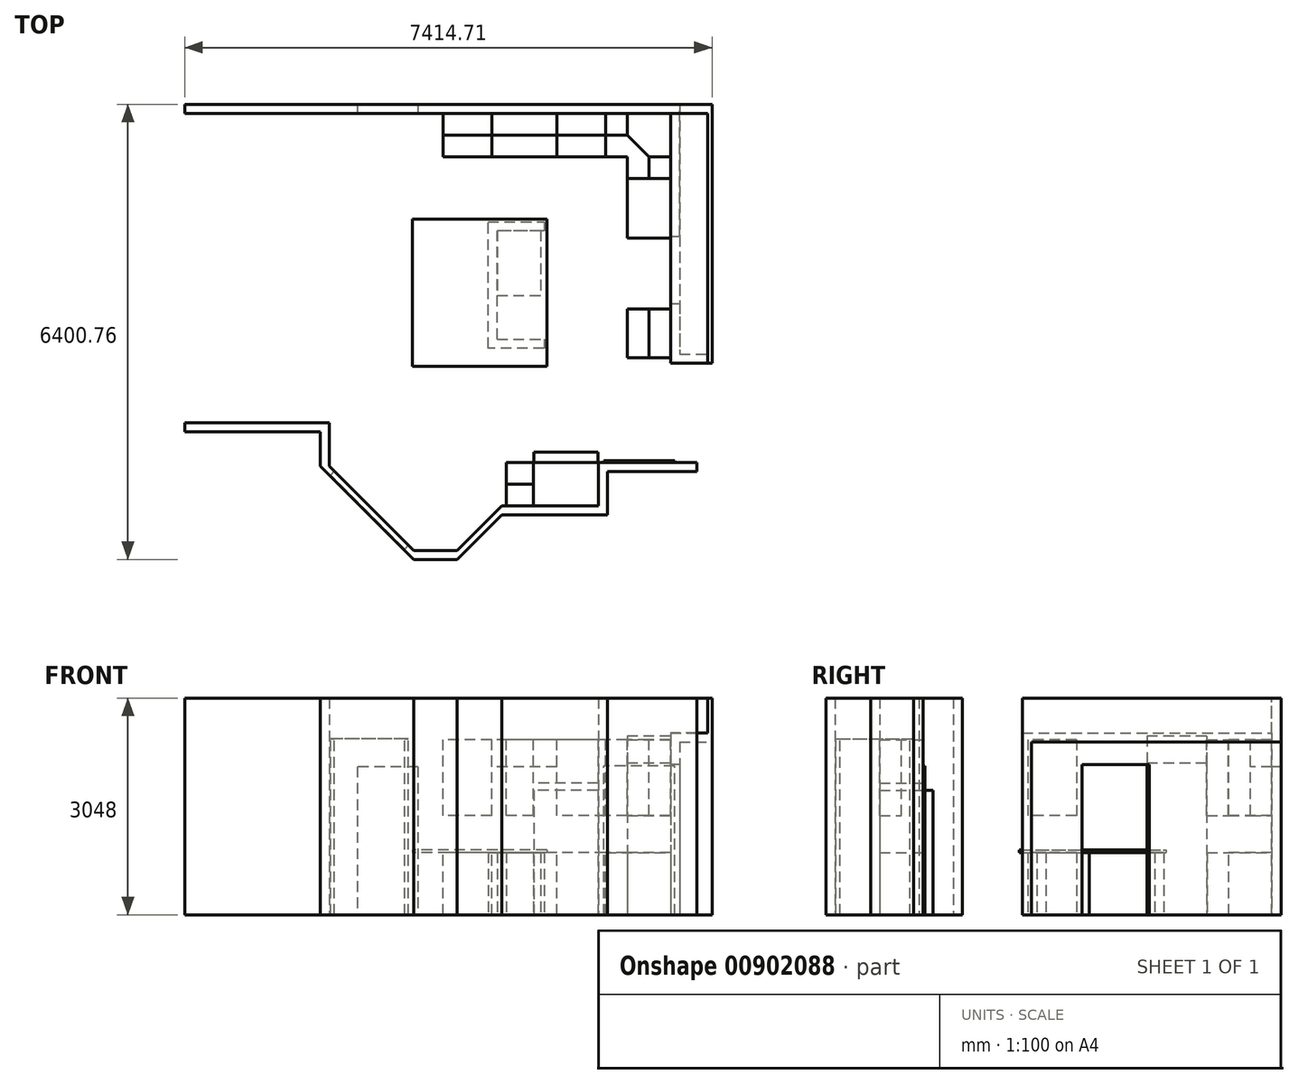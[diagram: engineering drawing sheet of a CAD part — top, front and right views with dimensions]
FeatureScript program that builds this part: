
annotation { "Feature Type Name" : "Feature", "Feature Type Description" : "" }
export const myFeature = defineFeature(function(context is Context, id is Id, definition is map)
    precondition{}
    {
        {
            var Q0;
            Q0=qCreatedBy(makeId("Top.planeOp"),FACE);
            var sketch = newSketch(context, id + "F0", { "sketchPlane" : qUnion([Q0])});
            skLineSegment(sketch, "E0.bottom", {"start": v(1769.95, -316.58) * mm, "end": v(-1786.05, -316.58) * mm});
            skLineSegment(sketch, "E0.top", {"start": v(1769.95, -189.58) * mm, "end": v(-1786.05, -189.58) * mm});
            skLineSegment(sketch, "E0.left", {"start": v(1769.95, -316.58) * mm, "end": v(1769.95, -189.58) * mm});
            skLineSegment(sketch, "E0.right", {"start": v(-1786.05, -316.58) * mm, "end": v(-1786.05, -189.58) * mm});
            skSolve(sketch);
        }
        {
            var Q0;
            Q0=qSketchRegion(id+"F0",true);
            extrude(context, id + "F1", {"entities" : qUnion([Q0]), "depth" : 3048 * mm, "offsetDistance" : 25.4 * mm});
        }
        {
            var Q0;
            Q0=makeQuery(id+"F1.opExtrude","CAP_FACE",FACE,{"disambiguationData":[OSD([sQuery(id+"F0.wireOp",EDGE,"E0.bottom"),sQuery(id+"F0.wireOp",EDGE,"E0.top"),sQuery(id+"F0.wireOp",EDGE,"E0.left"),sQuery(id+"F0.wireOp",EDGE,"E0.right")])],"isStart":true});
            var sketch = newSketch(context, id + "F2", { "sketchPlane" : qUnion([Q0])});
            skLineSegment(sketch, "E1", {"start": v(1769.95, 316.58) * mm, "end": v(1769.95, 2043.78) * mm});
            skLineSegment(sketch, "E2", {"start": v(1769.95, 2043.78) * mm, "end": v(1896.95, 2043.78) * mm});
            skLineSegment(sketch, "E3", {"start": v(1896.95, 2043.78) * mm, "end": v(1896.95, 189.58) * mm});
            skLineSegment(sketch, "E4", {"start": v(1896.95, 189.58) * mm, "end": v(1769.95, 189.58) * mm});
            skLineSegment(sketch, "E5", {"start": v(1769.95, 189.58) * mm, "end": v(1769.95, 316.58) * mm});
            skSolve(sketch);
        }
        {
            var Q0;
            Q0=makeQuery(id+"F2.imprint","IMPRINT",FACE,{"disambiguationData":[TD([[makeQuery(id+"F2.imprint","IMPRINT",EDGE,{"derivedFrom":sQuery(id+"F2.wireOp",EDGE,"E1")}),-1.0]])]});
            var Q1;
            Q1=makeQuery(id+"F1.opExtrude","CAP_FACE",FACE,{"disambiguationData":[OSD([sQuery(id+"F0.wireOp",EDGE,"E0.bottom"),sQuery(id+"F0.wireOp",EDGE,"E0.top"),sQuery(id+"F0.wireOp",EDGE,"E0.left"),sQuery(id+"F0.wireOp",EDGE,"E0.right")])],"isStart":false});
            extrude(context, id + "F3", {"entities" : qUnion([Q0]), "operationType" : NewBodyOperationType.ADD, "endBound" : BoundingType.UP_TO_SURFACE, "oppositeDirection" : true, "depth" : 25.4 * mm, "endBoundEntityFace" : qUnion([Q1]), "offsetDistance" : 25.4 * mm});
        }
        {
            var Q0;
            Q0=makeQuery(id+"F3.boolean.opBoolean","MERGE",FACE,{"derivedFrom":[makeQuery(id+"F1.opExtrude","CAP_FACE",FACE,{"disambiguationData":[OSD([sQuery(id+"F0.wireOp",EDGE,"E0.bottom"),sQuery(id+"F0.wireOp",EDGE,"E0.top"),sQuery(id+"F0.wireOp",EDGE,"E0.left"),sQuery(id+"F0.wireOp",EDGE,"E0.right")])],"isStart":true}),makeQuery(id+"F3.opExtrude","CAP_FACE",FACE,{"disambiguationData":[OSD([sQuery(id+"F2.wireOp",EDGE,"E1"),sQuery(id+"F2.wireOp",EDGE,"E2"),sQuery(id+"F2.wireOp",EDGE,"E3"),sQuery(id+"F2.wireOp",EDGE,"E4"),sQuery(id+"F2.wireOp",EDGE,"E5")])],"isStart":true})]});
            var sketch = newSketch(context, id + "F4", { "sketchPlane" : qUnion([Q0])});
            skLineSegment(sketch, "E6", {"start": v(1769.95, 2043.78) * mm, "end": v(1769.95, 3936.08) * mm, "construction": true});
            skLineSegment(sketch, "E7", {"start": v(1896.95, 2043.78) * mm, "end": v(1896.95, 4648.91) * mm, "construction": true});
            skLineSegment(sketch, "E8.bottom", {"start": v(1769.95, 2989.93) * mm, "end": v(1896.95, 2989.93) * mm});
            skLineSegment(sketch, "E8.top", {"start": v(1769.95, 3828.13) * mm, "end": v(1896.95, 3828.13) * mm});
            skLineSegment(sketch, "E8.left", {"start": v(1769.95, 2989.93) * mm, "end": v(1769.95, 3828.13) * mm});
            skLineSegment(sketch, "E8.right", {"start": v(1896.95, 2989.93) * mm, "end": v(1896.95, 3828.13) * mm});
            skSolve(sketch);
        }
        {
            var Q0;
            Q0=qSketchRegion(id+"F4",true);
            var Q1;
            Q1=makeQuery(id+"F3.boolean.opBoolean","MERGE",FACE,{"derivedFrom":[makeQuery(id+"F1.opExtrude","CAP_FACE",FACE,{"disambiguationData":[OSD([sQuery(id+"F0.wireOp",EDGE,"E0.bottom"),sQuery(id+"F0.wireOp",EDGE,"E0.top"),sQuery(id+"F0.wireOp",EDGE,"E0.left"),sQuery(id+"F0.wireOp",EDGE,"E0.right")])],"isStart":false}),makeQuery(id+"F3.opExtrude","CAP_FACE",FACE,{"disambiguationData":[OSD([sQuery(id+"F2.wireOp",EDGE,"E1"),sQuery(id+"F2.wireOp",EDGE,"E2"),sQuery(id+"F2.wireOp",EDGE,"E3"),sQuery(id+"F2.wireOp",EDGE,"E4"),sQuery(id+"F2.wireOp",EDGE,"E5")])],"isStart":false})]});
            extrude(context, id + "F5", {"entities" : qUnion([Q0]), "endBound" : BoundingType.UP_TO_SURFACE, "oppositeDirection" : true, "depth" : 25.4 * mm, "endBoundEntityFace" : qUnion([Q1]), "offsetDistance" : 25.4 * mm});
        }
        {
            var Q0;
            Q0=makeQuery(id+"F3.boolean.opBoolean","MERGE",FACE,{"derivedFrom":[makeQuery(id+"F1.opExtrude","CAP_FACE",FACE,{"disambiguationData":[OSD([sQuery(id+"F0.wireOp",EDGE,"E0.bottom"),sQuery(id+"F0.wireOp",EDGE,"E0.top"),sQuery(id+"F0.wireOp",EDGE,"E0.left"),sQuery(id+"F0.wireOp",EDGE,"E0.right")])],"isStart":true}),makeQuery(id+"F3.opExtrude","CAP_FACE",FACE,{"disambiguationData":[OSD([sQuery(id+"F2.wireOp",EDGE,"E1"),sQuery(id+"F2.wireOp",EDGE,"E2"),sQuery(id+"F2.wireOp",EDGE,"E3"),sQuery(id+"F2.wireOp",EDGE,"E4"),sQuery(id+"F2.wireOp",EDGE,"E5")])],"isStart":true})]});
            var sketch = newSketch(context, id + "F6", { "sketchPlane" : qUnion([Q0])});
            skLineSegment(sketch, "E9", {"start": v(1769.95, 2043.78) * mm, "end": v(1769.95, 3749.14) * mm, "construction": true});
            skLineSegment(sketch, "E10.bottom", {"start": v(1769.95, 5352.13) * mm, "end": v(753.95, 5352.13) * mm});
            skLineSegment(sketch, "E10.top", {"start": v(1769.95, 5225.13) * mm, "end": v(753.95, 5225.13) * mm});
            skLineSegment(sketch, "E10.left", {"start": v(1769.95, 5225.13) * mm, "end": v(1769.95, 5352.13) * mm});
            skLineSegment(sketch, "E10.right", {"start": v(753.95, 5225.13) * mm, "end": v(753.95, 5352.13) * mm});
            skSolve(sketch);
        }
        {
            var Q0;
            Q0=makeQuery(id+"F6.imprint","IMPRINT",FACE,{"disambiguationData":[TD([[makeQuery(id+"F6.imprint","IMPRINT",EDGE,{"derivedFrom":sQuery(id+"F6.wireOp",EDGE,"E10.bottom")}),1.0]])]});
            var Q1;
            Q1=makeQuery(id+"F3.boolean.opBoolean","MERGE",FACE,{"derivedFrom":[makeQuery(id+"F1.opExtrude","CAP_FACE",FACE,{"disambiguationData":[OSD([sQuery(id+"F0.wireOp",EDGE,"E0.bottom"),sQuery(id+"F0.wireOp",EDGE,"E0.top"),sQuery(id+"F0.wireOp",EDGE,"E0.left"),sQuery(id+"F0.wireOp",EDGE,"E0.right")])],"isStart":false}),makeQuery(id+"F3.opExtrude","CAP_FACE",FACE,{"disambiguationData":[OSD([sQuery(id+"F2.wireOp",EDGE,"E1"),sQuery(id+"F2.wireOp",EDGE,"E2"),sQuery(id+"F2.wireOp",EDGE,"E3"),sQuery(id+"F2.wireOp",EDGE,"E4"),sQuery(id+"F2.wireOp",EDGE,"E5")])],"isStart":false})]});
            extrude(context, id + "F7", {"entities" : qUnion([Q0]), "endBound" : BoundingType.UP_TO_SURFACE, "oppositeDirection" : true, "depth" : 25.4 * mm, "endBoundEntityFace" : qUnion([Q1]), "offsetDistance" : 25.4 * mm});
        }
        {
            var Q0;
            Q0=makeQuery(id+"F7.opExtrude","CAP_FACE",FACE,{"disambiguationData":[OSD([sQuery(id+"F6.wireOp",EDGE,"E10.bottom"),sQuery(id+"F6.wireOp",EDGE,"E10.top"),sQuery(id+"F6.wireOp",EDGE,"E10.left"),sQuery(id+"F6.wireOp",EDGE,"E10.right")])],"isStart":true});
            var sketch = newSketch(context, id + "F8", { "sketchPlane" : qUnion([Q0])});
            skLineSegment(sketch, "E11.bottom", {"start": v(753.95, 5225.13) * mm, "end": v(880.95, 5225.13) * mm});
            skLineSegment(sketch, "E11.top", {"start": v(753.95, 5834.73) * mm, "end": v(880.95, 5834.73) * mm});
            skLineSegment(sketch, "E11.left", {"start": v(753.95, 5225.13) * mm, "end": v(753.95, 5834.73) * mm});
            skLineSegment(sketch, "E11.right", {"start": v(880.95, 5225.13) * mm, "end": v(880.95, 5834.73) * mm});
            skLineSegment(sketch, "E12.bottom", {"start": v(880.95, 5834.73) * mm, "end": v(-604.95, 5834.73) * mm});
            skLineSegment(sketch, "E12.top", {"start": v(880.95, 5961.73) * mm, "end": v(-604.95, 5961.73) * mm});
            skLineSegment(sketch, "E12.left", {"start": v(880.95, 5834.73) * mm, "end": v(880.95, 5961.73) * mm});
            skLineSegment(sketch, "E12.right", {"start": v(-604.95, 5834.73) * mm, "end": v(-604.95, 5961.73) * mm});
            skLineSegment(sketch, "E13", {"start": v(-604.95, 5834.73) * mm, "end": v(-1233.57, 6463.34) * mm});
            skLineSegment(sketch, "E14", {"start": v(-1233.57, 6463.34) * mm, "end": v(-1843.17, 6463.34) * mm});
            skLineSegment(sketch, "E15", {"start": v(-1843.17, 6463.34) * mm, "end": v(-1843.17, 6590.34) * mm});
            skLineSegment(sketch, "E16", {"start": v(-1843.17, 6590.34) * mm, "end": v(-1233.57, 6590.34) * mm});
            skLineSegment(sketch, "E17", {"start": v(-1233.57, 6590.34) * mm, "end": v(-604.95, 5961.73) * mm});
            skLineSegment(sketch, "E18", {"start": v(-1843.17, 6463.34) * mm, "end": v(-3028.56, 5277.95) * mm});
            skLineSegment(sketch, "E19", {"start": v(-3028.56, 5277.95) * mm, "end": v(-3028.56, 4668.35) * mm});
            skLineSegment(sketch, "E20", {"start": v(-3028.56, 4668.35) * mm, "end": v(-5060.56, 4668.35) * mm});
            skLineSegment(sketch, "E21", {"start": v(-5060.56, 4668.35) * mm, "end": v(-5060.56, 4795.35) * mm});
            skLineSegment(sketch, "E22", {"start": v(-5060.56, 4795.35) * mm, "end": v(-3155.56, 4795.35) * mm});
            skLineSegment(sketch, "E23", {"start": v(-3155.56, 4795.35) * mm, "end": v(-3155.56, 5277.95) * mm});
            skLineSegment(sketch, "E24", {"start": v(-3155.56, 5277.95) * mm, "end": v(-1843.17, 6590.34) * mm});
            skSolve(sketch);
        }
        {
            var Q0;
            Q0=makeQuery(id+"F8.imprint","IMPRINT",FACE,{"disambiguationData":[TD([[makeQuery(id+"F8.imprint","IMPRINT",EDGE,{"derivedFrom":sQuery(id+"F8.wireOp",EDGE,"E15")}),1.0]])]});
            var Q1;
            Q1=makeQuery(id+"F8.imprint","IMPRINT",FACE,{"disambiguationData":[TD([[makeQuery(id+"F8.imprint","IMPRINT",EDGE,{"derivedFrom":sQuery(id+"F8.wireOp",EDGE,"E12.right")}),1.0]])]});
            var Q2;
            Q2=makeQuery(id+"F8.imprint","IMPRINT",FACE,{"disambiguationData":[TD([[makeQuery(id+"F8.imprint","IMPRINT",EDGE,{"derivedFrom":sQuery(id+"F8.wireOp",EDGE,"E12.top")}),1.0]])]});
            var Q3;
            {var subQ0=sQuery(id+"F8.wireOp",EDGE,"E11.left");var subQ1=makeQuery(id+"F7.opExtrude","CAP_EDGE",EDGE,{"disambiguationData":[OSD([sQuery(id+"F6.wireOp",EDGE,"E10.bottom")])],"isStart":true});var subQ2=makeQuery(id+"F8.imprint","INTERSECT",VERTEX,{"derivedFrom":[subQ1,subQ0]});Q3=makeQuery(id+"F8.imprint","IMPRINT",FACE,{"disambiguationData":[TD([[makeQuery(id+"F8.imprint","IMPRINT",EDGE,{"disambiguationData":[TD([[subQ2,-1.0]])],"derivedFrom":subQ0}),-1.0]])]});}
            var Q4;
            Q4=makeQuery(id+"F5.opExtrude","CAP_FACE",FACE,{"disambiguationData":[OSD([sQuery(id+"F4.wireOp",EDGE,"E8.bottom"),sQuery(id+"F4.wireOp",EDGE,"E8.top"),sQuery(id+"F4.wireOp",EDGE,"E8.left"),sQuery(id+"F4.wireOp",EDGE,"E8.right")])],"isStart":false});
            extrude(context, id + "F9", {"entities" : qUnion([Q0, Q1, Q2, Q3]), "operationType" : NewBodyOperationType.ADD, "endBound" : BoundingType.UP_TO_SURFACE, "oppositeDirection" : true, "depth" : 25.4 * mm, "endBoundEntityFace" : qUnion([Q4]), "offsetDistance" : 25.4 * mm});
        }
        {
            var Q0;
            {var subQ0=sQuery(id+"F6.wireOp",EDGE,"E10.bottom");Q0=makeQuery(id+"F9.boolean.opBoolean","MERGE",FACE,{"derivedFrom":[makeQuery(id+"F7.opExtrude","CAP_FACE",FACE,{"disambiguationData":[OSD([subQ0,sQuery(id+"F6.wireOp",EDGE,"E10.top"),sQuery(id+"F6.wireOp",EDGE,"E10.left"),sQuery(id+"F6.wireOp",EDGE,"E10.right")])],"isStart":true}),makeQuery(id+"F9.opExtrude","CAP_FACE",FACE,{"disambiguationData":[OSD([subQ0,sQuery(id+"F8.wireOp",EDGE,"E11.left"),sQuery(id+"F8.wireOp",EDGE,"E11.right"),sQuery(id+"F8.wireOp",EDGE,"E12.bottom"),sQuery(id+"F8.wireOp",EDGE,"E12.top"),sQuery(id+"F8.wireOp",EDGE,"E12.left"),sQuery(id+"F8.wireOp",EDGE,"E13"),sQuery(id+"F8.wireOp",EDGE,"E14"),sQuery(id+"F8.wireOp",EDGE,"E16"),sQuery(id+"F8.wireOp",EDGE,"E17"),sQuery(id+"F8.wireOp",EDGE,"E18"),sQuery(id+"F8.wireOp",EDGE,"E19"),sQuery(id+"F8.wireOp",EDGE,"E20"),sQuery(id+"F8.wireOp",EDGE,"E21"),sQuery(id+"F8.wireOp",EDGE,"E22"),sQuery(id+"F8.wireOp",EDGE,"E23"),sQuery(id+"F8.wireOp",EDGE,"E24")])],"isStart":true})]});}
            var sketch = newSketch(context, id + "F10", { "sketchPlane" : qUnion([Q0])});
            skLineSegment(sketch, "E25.bottom", {"start": v(1769.95, 5225.13) * mm, "end": v(2138.25, 5225.13) * mm});
            skLineSegment(sketch, "E25.top", {"start": v(1769.95, 5352.13) * mm, "end": v(2138.25, 5352.13) * mm});
            skLineSegment(sketch, "E25.left", {"start": v(1769.95, 5225.13) * mm, "end": v(1769.95, 5352.13) * mm});
            skLineSegment(sketch, "E25.right", {"start": v(2138.25, 5225.13) * mm, "end": v(2138.25, 5352.13) * mm});
            skSolve(sketch);
        }
        {
            var Q0;
            Q0=makeQuery(id+"F10.imprint","IMPRINT",FACE,{"disambiguationData":[TD([[makeQuery(id+"F10.imprint","IMPRINT",EDGE,{"derivedFrom":sQuery(id+"F10.wireOp",EDGE,"E25.bottom")}),1.0]])]});
            var Q1;
            {var subQ0=sQuery(id+"F6.wireOp",EDGE,"E10.bottom");Q1=makeQuery(id+"F9.boolean.opBoolean","MERGE",FACE,{"derivedFrom":[makeQuery(id+"F7.opExtrude","CAP_FACE",FACE,{"disambiguationData":[OSD([subQ0,sQuery(id+"F6.wireOp",EDGE,"E10.top"),sQuery(id+"F6.wireOp",EDGE,"E10.left"),sQuery(id+"F6.wireOp",EDGE,"E10.right")])],"isStart":false}),makeQuery(id+"F9.opExtrude","CAP_FACE",FACE,{"disambiguationData":[OSD([subQ0,sQuery(id+"F8.wireOp",EDGE,"E11.left"),sQuery(id+"F8.wireOp",EDGE,"E11.right"),sQuery(id+"F8.wireOp",EDGE,"E12.bottom"),sQuery(id+"F8.wireOp",EDGE,"E12.top"),sQuery(id+"F8.wireOp",EDGE,"E12.left"),sQuery(id+"F8.wireOp",EDGE,"E13"),sQuery(id+"F8.wireOp",EDGE,"E14"),sQuery(id+"F8.wireOp",EDGE,"E16"),sQuery(id+"F8.wireOp",EDGE,"E17"),sQuery(id+"F8.wireOp",EDGE,"E18"),sQuery(id+"F8.wireOp",EDGE,"E19"),sQuery(id+"F8.wireOp",EDGE,"E20"),sQuery(id+"F8.wireOp",EDGE,"E21"),sQuery(id+"F8.wireOp",EDGE,"E22"),sQuery(id+"F8.wireOp",EDGE,"E23"),sQuery(id+"F8.wireOp",EDGE,"E24")])],"isStart":false})]});}
            extrude(context, id + "F11", {"entities" : qUnion([Q0]), "operationType" : NewBodyOperationType.ADD, "endBound" : BoundingType.UP_TO_SURFACE, "oppositeDirection" : true, "depth" : 25.4 * mm, "endBoundEntityFace" : qUnion([Q1]), "offsetDistance" : 25.4 * mm});
        }
        {
            var Q0;
            Q0=makeQuery(id+"F11.boolean.opBoolean","MERGE",FACE,{"derivedFrom":[makeQuery(id+"F7.opExtrude","SWEPT_FACE",FACE,{"disambiguationData":[OSD([sQuery(id+"F6.wireOp",EDGE,"E10.top")])]}),makeQuery(id+"F11.opExtrude","SWEPT_FACE",FACE,{"disambiguationData":[OSD([sQuery(id+"F10.wireOp",EDGE,"E25.bottom")])]})]});
            var sketch = newSketch(context, id + "F12", { "sketchPlane" : qUnion([Q0])});
            skLineSegment(sketch, "E26.bottom", {"start": v(-1827.1, 0) * mm, "end": v(-830.15, 0) * mm});
            skLineSegment(sketch, "E26.top", {"start": v(-1827.1, 2095.5) * mm, "end": v(-830.15, 2095.5) * mm});
            skLineSegment(sketch, "E26.left", {"start": v(-1827.1, 0) * mm, "end": v(-1827.1, 2095.5) * mm});
            skLineSegment(sketch, "E26.right", {"start": v(-830.15, 0) * mm, "end": v(-830.15, 2095.5) * mm});
            skSolve(sketch);
        }
        {
            var Q0;
            Q0=qSketchRegion(id+"F12",true);
            extrude(context, id + "F13", {"entities" : qUnion([Q0]), "operationType" : NewBodyOperationType.ADD, "depth" : 25.4 * mm, "offsetDistance" : 25.4 * mm});
        }
        {
            var Q0;
            Q0=makeQuery(id+"F1.opExtrude","SWEPT_FACE",FACE,{"disambiguationData":[OSD([sQuery(id+"F0.wireOp",EDGE,"E0.bottom")])]});
            var sketch = newSketch(context, id + "F14", { "sketchPlane" : qUnion([Q0])});
            skLineSegment(sketch, "E27.bottom", {"start": v(-1786.05, 3048) * mm, "end": v(-2636.95, 3048) * mm});
            skLineSegment(sketch, "E27.top", {"start": v(-1786.05, 2082.8) * mm, "end": v(-2636.95, 2082.8) * mm});
            skLineSegment(sketch, "E27.left", {"start": v(-1786.05, 3048) * mm, "end": v(-1786.05, 2082.8) * mm});
            skLineSegment(sketch, "E27.right", {"start": v(-2636.95, 3048) * mm, "end": v(-2636.95, 2082.8) * mm});
            skSolve(sketch);
        }
        {
            var Q0;
            Q0=makeQuery(id+"F14.imprint","IMPRINT",FACE,{"disambiguationData":[TD([[makeQuery(id+"F14.imprint","IMPRINT",EDGE,{"derivedFrom":sQuery(id+"F14.wireOp",EDGE,"E27.bottom")}),1.0]])]});
            var Q1;
            Q1=makeQuery(id+"F3.boolean.opBoolean","MERGE",FACE,{"derivedFrom":[makeQuery(id+"F1.opExtrude","SWEPT_FACE",FACE,{"disambiguationData":[OSD([sQuery(id+"F0.wireOp",EDGE,"E0.top")])]}),makeQuery(id+"F3.opExtrude","SWEPT_FACE",FACE,{"disambiguationData":[OSD([sQuery(id+"F2.wireOp",EDGE,"E4")])]})]});
            extrude(context, id + "F15", {"entities" : qUnion([Q0]), "operationType" : NewBodyOperationType.ADD, "endBound" : BoundingType.UP_TO_SURFACE, "oppositeDirection" : true, "depth" : 25.4 * mm, "endBoundEntityFace" : qUnion([Q1]), "offsetDistance" : 25.4 * mm});
        }
        {
            var Q0;
            Q0=makeQuery(id+"F15.opExtrude","SWEPT_FACE",FACE,{"disambiguationData":[OSD([sQuery(id+"F14.wireOp",EDGE,"E27.right")])]});
            var sketch = newSketch(context, id + "F16", { "sketchPlane" : qUnion([Q0])});
            skLineSegment(sketch, "E28.bottom", {"start": v(189.58, 3048) * mm, "end": v(316.58, 3048) * mm});
            skLineSegment(sketch, "E28.top", {"start": v(189.58, 0) * mm, "end": v(316.58, 0) * mm});
            skLineSegment(sketch, "E28.left", {"start": v(189.58, 3048) * mm, "end": v(189.58, 0) * mm});
            skLineSegment(sketch, "E28.right", {"start": v(316.58, 3048) * mm, "end": v(316.58, 0) * mm});
            skSolve(sketch);
        }
        {
            var Q0;
            {var subQ0=sQuery(id+"F16.wireOp",EDGE,"E28.bottom");Q0=makeQuery(id+"F16.imprint","IMPRINT",FACE,{"disambiguationData":[TD([[makeQuery(id+"F16.imprint","IMPRINT",EDGE,{"derivedFrom":subQ0}),-1.0]])]});}
            var Q1;
            {var subQ0=sQuery(id+"F16.wireOp",EDGE,"E28.top");Q1=makeQuery(id+"F16.imprint","IMPRINT",FACE,{"disambiguationData":[TD([[makeQuery(id+"F16.imprint","IMPRINT",EDGE,{"derivedFrom":subQ0}),1.0]])]});}
            var Q2;
            Q2=makeQuery(id+"F9.opExtrude","SWEPT_FACE",FACE,{"disambiguationData":[OSD([sQuery(id+"F8.wireOp",EDGE,"E21")])]});
            extrude(context, id + "F17", {"entities" : qUnion([Q0, Q1]), "operationType" : NewBodyOperationType.ADD, "endBound" : BoundingType.UP_TO_SURFACE, "depth" : 25.4 * mm, "endBoundEntityFace" : qUnion([Q2]), "offsetDistance" : 25.4 * mm});
        }
        {
            var Q0;
            Q0=makeQuery(id+"F3.opExtrude","SWEPT_FACE",FACE,{"disambiguationData":[OSD([sQuery(id+"F2.wireOp",EDGE,"E1"),sQuery(id+"F2.wireOp",EDGE,"E5")])]});
            var sketch = newSketch(context, id + "F18", { "sketchPlane" : qUnion([Q0])});
            skLineSegment(sketch, "E29.bottom", {"start": v(2043.78, 3048) * mm, "end": v(3103.37, 3048) * mm});
            skLineSegment(sketch, "E29.top", {"start": v(2043.78, 2114.55) * mm, "end": v(3103.37, 2114.55) * mm});
            skLineSegment(sketch, "E29.left", {"start": v(2043.78, 3048) * mm, "end": v(2043.78, 2114.55) * mm});
            skLineSegment(sketch, "E29.right", {"start": v(3103.37, 3048) * mm, "end": v(3103.37, 2114.55) * mm});
            skSolve(sketch);
        }
        {
            var Q0;
            Q0=makeQuery(id+"F18.imprint","IMPRINT",FACE,{"disambiguationData":[TD([[makeQuery(id+"F18.imprint","IMPRINT",EDGE,{"derivedFrom":sQuery(id+"F18.wireOp",EDGE,"E29.bottom")}),-1.0]])]});
            var Q1;
            Q1=makeQuery(id+"F5.opExtrude","SWEPT_FACE",FACE,{"disambiguationData":[OSD([sQuery(id+"F4.wireOp",EDGE,"E8.right")])]});
            extrude(context, id + "F19", {"entities" : qUnion([Q0]), "endBound" : BoundingType.UP_TO_SURFACE, "oppositeDirection" : true, "depth" : 25.4 * mm, "endBoundEntityFace" : qUnion([Q1]), "offsetDistance" : 25.4 * mm});
        }
        {
            var Q0;
            Q0=makeQuery(id+"F1.opExtrude","SWEPT_BODY",BODY,{"disambiguationData":[OSD([sQuery(id+"F0.wireOp",EDGE,"E0.bottom"),sQuery(id+"F0.wireOp",EDGE,"E0.top"),sQuery(id+"F0.wireOp",EDGE,"E0.left"),sQuery(id+"F0.wireOp",EDGE,"E0.right")])]});
            var Q1;
            Q1=makeQuery(id+"F19.opExtrude","SWEPT_BODY",BODY,{"disambiguationData":[OSD([sQuery(id+"F18.wireOp",EDGE,"E29.bottom"),sQuery(id+"F18.wireOp",EDGE,"E29.top"),sQuery(id+"F18.wireOp",EDGE,"E29.left"),sQuery(id+"F18.wireOp",EDGE,"E29.right")])]});
            var Q2;
            Q2=makeQuery(id+"F5.opExtrude","SWEPT_BODY",BODY,{"disambiguationData":[OSD([sQuery(id+"F4.wireOp",EDGE,"E8.bottom"),sQuery(id+"F4.wireOp",EDGE,"E8.top"),sQuery(id+"F4.wireOp",EDGE,"E8.left"),sQuery(id+"F4.wireOp",EDGE,"E8.right")])]});
            booleanBodies(context, id + "F20", {"operationType" : BooleanOperationType.UNION, "tools" : qUnion([Q0, Q1, Q2])});
        }
        {
            var Q0;
            Q0=makeQuery(id+"F20.opBoolean","MERGE",FACE,{"derivedFrom":[makeQuery(id+"F5.opExtrude","CAP_FACE",FACE,{"disambiguationData":[OSD([sQuery(id+"F4.wireOp",EDGE,"E8.bottom"),sQuery(id+"F4.wireOp",EDGE,"E8.top"),sQuery(id+"F4.wireOp",EDGE,"E8.left"),sQuery(id+"F4.wireOp",EDGE,"E8.right")])],"isStart":false}),makeQuery(id+"F17.boolean.opBoolean","MERGE",FACE,{"derivedFrom":[makeQuery(id+"F15.boolean.opBoolean","MERGE",FACE,{"derivedFrom":[makeQuery(id+"F3.boolean.opBoolean","MERGE",FACE,{"derivedFrom":[makeQuery(id+"F1.opExtrude","CAP_FACE",FACE,{"disambiguationData":[OSD([sQuery(id+"F0.wireOp",EDGE,"E0.bottom"),sQuery(id+"F0.wireOp",EDGE,"E0.top"),sQuery(id+"F0.wireOp",EDGE,"E0.left"),sQuery(id+"F0.wireOp",EDGE,"E0.right")])],"isStart":false}),makeQuery(id+"F3.opExtrude","CAP_FACE",FACE,{"disambiguationData":[OSD([sQuery(id+"F2.wireOp",EDGE,"E1"),sQuery(id+"F2.wireOp",EDGE,"E2"),sQuery(id+"F2.wireOp",EDGE,"E3"),sQuery(id+"F2.wireOp",EDGE,"E4"),sQuery(id+"F2.wireOp",EDGE,"E5")])],"isStart":false})]}),makeQuery(id+"F15.opExtrude","SWEPT_FACE",FACE,{"disambiguationData":[OSD([sQuery(id+"F14.wireOp",EDGE,"E27.bottom")])]})]}),makeQuery(id+"F17.opExtrude","SWEPT_FACE",FACE,{"disambiguationData":[OSD([sQuery(id+"F16.wireOp",EDGE,"E28.bottom")])]})]}),makeQuery(id+"F19.opExtrude","SWEPT_FACE",FACE,{"disambiguationData":[OSD([sQuery(id+"F18.wireOp",EDGE,"E29.bottom")])]})]});
            var sketch = newSketch(context, id + "F21", { "sketchPlane" : qUnion([Q0])});
            skLineSegment(sketch, "E30.bottom", {"start": v(1769.95, -3828.13) * mm, "end": v(2354.15, -3828.13) * mm});
            skLineSegment(sketch, "E30.top", {"start": v(1769.95, -3701.13) * mm, "end": v(2354.15, -3701.13) * mm});
            skLineSegment(sketch, "E30.left", {"start": v(1769.95, -3828.13) * mm, "end": v(1769.95, -3701.13) * mm});
            skLineSegment(sketch, "E30.right", {"start": v(2354.15, -3828.13) * mm, "end": v(2354.15, -3701.13) * mm});
            skSolve(sketch);
        }
        {
            var Q0;
            {var subQ3=sQuery(id+"F21.wireOp",EDGE,"E30.right");Q0=makeQuery(id+"F21.imprint","IMPRINT",FACE,{"disambiguationData":[TD([[makeQuery(id+"F21.imprint","IMPRINT",EDGE,{"derivedFrom":subQ3}),1.0]])]});}
            var Q1;
            Q1=makeQuery(id+"F5.opExtrude","CAP_FACE",FACE,{"disambiguationData":[OSD([sQuery(id+"F4.wireOp",EDGE,"E8.bottom"),sQuery(id+"F4.wireOp",EDGE,"E8.top"),sQuery(id+"F4.wireOp",EDGE,"E8.left"),sQuery(id+"F4.wireOp",EDGE,"E8.right")])],"isStart":true});
            extrude(context, id + "F22", {"entities" : qUnion([Q0]), "operationType" : NewBodyOperationType.ADD, "endBound" : BoundingType.UP_TO_SURFACE, "oppositeDirection" : true, "depth" : 25.4 * mm, "endBoundEntityFace" : qUnion([Q1]), "offsetDistance" : 25.4 * mm});
        }
        {
            var Q0;
            Q0=makeQuery(id+"F19.opExtrude","SWEPT_FACE",FACE,{"disambiguationData":[OSD([sQuery(id+"F18.wireOp",EDGE,"E29.top")])]});
            cPlane(context, id + "F23", {"entities" : qUnion([Q0]), "cplaneType" : CPlaneType.OFFSET, "offset" : 444.5 * mm, "oppositeDirection" : true, "width" : 152.4 * mm, "height" : 152.4 * mm});
        }
        {
            var Q0;
            Q0=qCreatedBy(id+"F23.planeOp",FACE);
            var sketch = newSketch(context, id + "F24", { "sketchPlane" : qUnion([Q0])});
            skLineSegment(sketch, "E31.bottom", {"start": v(1769.95, 3828.13) * mm, "end": v(2290.65, 3828.13) * mm});
            skLineSegment(sketch, "E31.top", {"start": v(1769.95, 189.58) * mm, "end": v(2290.65, 189.58) * mm});
            skLineSegment(sketch, "E31.left", {"start": v(1769.95, 3828.13) * mm, "end": v(1769.95, 189.58) * mm});
            skLineSegment(sketch, "E31.right", {"start": v(2290.65, 3828.13) * mm, "end": v(2290.65, 189.58) * mm});
            skSolve(sketch);
        }
        {
            var Q0;
            Q0=makeQuery(id+"F24.imprint","IMPRINT",FACE,{"disambiguationData":[TD([[makeQuery(id+"F24.imprint","IMPRINT",EDGE,{"derivedFrom":sQuery(id+"F24.wireOp",EDGE,"E31.bottom")}),-1.0]])]});
            extrude(context, id + "F25", {"entities" : qUnion([Q0]), "operationType" : NewBodyOperationType.ADD, "depth" : 127 * mm, "offsetDistance" : 25.4 * mm});
        }
        {
            var Q0;
            Q0=makeQuery(id+"F25.opExtrude","SWEPT_FACE",FACE,{"disambiguationData":[OSD([sQuery(id+"F24.wireOp",EDGE,"E31.right")])]});
            var sketch = newSketch(context, id + "F26", { "sketchPlane" : qUnion([Q0])});
            skLineSegment(sketch, "E32.bottom", {"start": v(-4015.8, 2559.05) * mm, "end": v(-316.58, 2559.05) * mm});
            skLineSegment(sketch, "E32.top", {"start": v(-4015.8, 4185.07) * mm, "end": v(-316.58, 4185.07) * mm});
            skLineSegment(sketch, "E32.left", {"start": v(-4015.8, 2559.05) * mm, "end": v(-4015.8, 4185.07) * mm});
            skLineSegment(sketch, "E32.right", {"start": v(-316.58, 2559.05) * mm, "end": v(-316.58, 4185.07) * mm});
            skSolve(sketch);
        }
        {
            var Q0;
            Q0=qSketchRegion(id+"F26",true);
            extrude(context, id + "F27", {"entities" : qUnion([Q0]), "operationType" : NewBodyOperationType.REMOVE, "oppositeDirection" : true, "depth" : 1270 * mm, "offsetDistance" : 25.4 * mm});
        }
        {
            var Q0;
            Q0=makeQuery(id+"F25.boolean.opBoolean","MERGE",FACE,{"derivedFrom":[makeQuery(id+"F17.boolean.opBoolean","MERGE",FACE,{"derivedFrom":[makeQuery(id+"F15.boolean.opBoolean","MERGE",FACE,{"derivedFrom":[makeQuery(id+"F3.boolean.opBoolean","MERGE",FACE,{"derivedFrom":[makeQuery(id+"F1.opExtrude","SWEPT_FACE",FACE,{"disambiguationData":[OSD([sQuery(id+"F0.wireOp",EDGE,"E0.top")])]}),makeQuery(id+"F3.opExtrude","SWEPT_FACE",FACE,{"disambiguationData":[OSD([sQuery(id+"F2.wireOp",EDGE,"E4")])]})]}),makeQuery(id+"F15.opExtrude","CAP_FACE",FACE,{"disambiguationData":[OSD([sQuery(id+"F14.wireOp",EDGE,"E27.bottom"),sQuery(id+"F14.wireOp",EDGE,"E27.top"),sQuery(id+"F14.wireOp",EDGE,"E27.left"),sQuery(id+"F14.wireOp",EDGE,"E27.right")])],"isStart":false})]}),makeQuery(id+"F17.opExtrude","SWEPT_FACE",FACE,{"disambiguationData":[OSD([sQuery(id+"F16.wireOp",EDGE,"E28.left")])]})]}),makeQuery(id+"F25.opExtrude","SWEPT_FACE",FACE,{"disambiguationData":[OSD([sQuery(id+"F24.wireOp",EDGE,"E31.top")])]})]});
            var sketch = newSketch(context, id + "F28", { "sketchPlane" : qUnion([Q0])});
            skLineSegment(sketch, "E33.bottom", {"start": v(-1896.95, 3048) * mm, "end": v(-2354.15, 3048) * mm});
            skLineSegment(sketch, "E33.top", {"start": v(-1896.95, 2432.05) * mm, "end": v(-2354.15, 2432.05) * mm});
            skLineSegment(sketch, "E33.left", {"start": v(-1896.95, 3048) * mm, "end": v(-1896.95, 2432.05) * mm});
            skLineSegment(sketch, "E33.right", {"start": v(-2354.15, 3048) * mm, "end": v(-2354.15, 2432.05) * mm});
            skSolve(sketch);
        }
        {
            var Q0;
            {var subQ1=sQuery(id+"F28.wireOp",EDGE,"E33.bottom");Q0=makeQuery(id+"F28.imprint","IMPRINT",FACE,{"disambiguationData":[TD([[makeQuery(id+"F28.imprint","IMPRINT",EDGE,{"derivedFrom":subQ1}),1.0]])]});}
            var Q1;
            Q1=makeQuery(id+"F27.boolean.opBoolean","MERGE",FACE,{"derivedFrom":[makeQuery(id+"F17.boolean.opBoolean","MERGE",FACE,{"derivedFrom":[makeQuery(id+"F15.boolean.opBoolean","MERGE",FACE,{"derivedFrom":[makeQuery(id+"F1.opExtrude","SWEPT_FACE",FACE,{"disambiguationData":[OSD([sQuery(id+"F0.wireOp",EDGE,"E0.bottom")])]}),makeQuery(id+"F15.opExtrude","CAP_FACE",FACE,{"disambiguationData":[OSD([sQuery(id+"F14.wireOp",EDGE,"E27.bottom"),sQuery(id+"F14.wireOp",EDGE,"E27.top"),sQuery(id+"F14.wireOp",EDGE,"E27.left"),sQuery(id+"F14.wireOp",EDGE,"E27.right")])],"isStart":true})]}),makeQuery(id+"F17.opExtrude","SWEPT_FACE",FACE,{"disambiguationData":[OSD([sQuery(id+"F16.wireOp",EDGE,"E28.right")])]})]})],"fromTools":[makeQuery(id+"F27.opExtrude","SWEPT_FACE",FACE,{"disambiguationData":[OSD([sQuery(id+"F26.wireOp",EDGE,"E32.right")])]})]});
            extrude(context, id + "F29", {"entities" : qUnion([Q0]), "operationType" : NewBodyOperationType.ADD, "endBound" : BoundingType.UP_TO_SURFACE, "oppositeDirection" : true, "depth" : 25.4 * mm, "endBoundEntityFace" : qUnion([Q1]), "offsetDistance" : 25.4 * mm});
        }
        {
            var Q0;
            {var subQ0=sQuery(id+"F24.wireOp",EDGE,"E31.top");Q0=makeQuery(id+"F29.boolean.opBoolean","MERGE",FACE,{"derivedFrom":[makeQuery(id+"F25.boolean.opBoolean","MERGE",FACE,{"derivedFrom":[makeQuery(id+"F17.boolean.opBoolean","MERGE",FACE,{"derivedFrom":[makeQuery(id+"F15.boolean.opBoolean","MERGE",FACE,{"derivedFrom":[makeQuery(id+"F3.boolean.opBoolean","MERGE",FACE,{"derivedFrom":[makeQuery(id+"F1.opExtrude","SWEPT_FACE",FACE,{"disambiguationData":[OSD([sQuery(id+"F0.wireOp",EDGE,"E0.top")])]}),makeQuery(id+"F3.opExtrude","SWEPT_FACE",FACE,{"disambiguationData":[OSD([sQuery(id+"F2.wireOp",EDGE,"E4")])]})]}),makeQuery(id+"F15.opExtrude","CAP_FACE",FACE,{"disambiguationData":[OSD([sQuery(id+"F14.wireOp",EDGE,"E27.bottom"),sQuery(id+"F14.wireOp",EDGE,"E27.top"),sQuery(id+"F14.wireOp",EDGE,"E27.left"),sQuery(id+"F14.wireOp",EDGE,"E27.right")])],"isStart":false})]}),makeQuery(id+"F17.opExtrude","SWEPT_FACE",FACE,{"disambiguationData":[OSD([sQuery(id+"F16.wireOp",EDGE,"E28.left")])]})]}),makeQuery(id+"F25.opExtrude","SWEPT_FACE",FACE,{"disambiguationData":[OSD([subQ0])]})]}),makeQuery(id+"F29.opExtrude","CAP_FACE",FACE,{"disambiguationData":[OSD([subQ0,sQuery(id+"F24.wireOp",EDGE,"E31.right"),sQuery(id+"F28.wireOp",EDGE,"E33.bottom"),sQuery(id+"F28.wireOp",EDGE,"E33.top"),sQuery(id+"F28.wireOp",EDGE,"E33.left"),sQuery(id+"F28.wireOp",EDGE,"E33.right")])],"isStart":true})]});}
            var sketch = newSketch(context, id + "F30", { "sketchPlane" : qUnion([Q0])});
            skLineSegment(sketch, "E34.bottom", {"start": v(-2354.15, 3048) * mm, "end": v(-2290.65, 3048) * mm});
            skLineSegment(sketch, "E34.top", {"start": v(-2354.15, 2432.05) * mm, "end": v(-2290.65, 2432.05) * mm});
            skLineSegment(sketch, "E34.left", {"start": v(-2354.15, 3048) * mm, "end": v(-2354.15, 2432.05) * mm});
            skLineSegment(sketch, "E34.right", {"start": v(-2290.65, 3048) * mm, "end": v(-2290.65, 2432.05) * mm});
            skSolve(sketch);
        }
        {
            var Q0;
            Q0=makeQuery(id+"F30.imprint","IMPRINT",FACE,{"disambiguationData":[TD([[makeQuery(id+"F30.imprint","IMPRINT",EDGE,{"derivedFrom":sQuery(id+"F30.wireOp",EDGE,"E34.bottom")}),-1.0]])]});
            var Q1;
            Q1=makeQuery(id+"F22.opExtrude","SWEPT_FACE",FACE,{"disambiguationData":[OSD([sQuery(id+"F21.wireOp",EDGE,"E30.top")])]});
            extrude(context, id + "F31", {"entities" : qUnion([Q0]), "operationType" : NewBodyOperationType.ADD, "endBound" : BoundingType.UP_TO_SURFACE, "oppositeDirection" : true, "depth" : 25.4 * mm, "endBoundEntityFace" : qUnion([Q1]), "offsetDistance" : 25.4 * mm});
        }
        {
            var Q0;
            Q0=makeQuery(id+"F9.opExtrude","SWEPT_FACE",FACE,{"disambiguationData":[OSD([sQuery(id+"F8.wireOp",EDGE,"E18")])]});
            var sketch = newSketch(context, id + "F32", { "sketchPlane" : qUnion([Q0])});
            skLineSegment(sketch, "E35.bottom", {"start": v(-3165.36, 0) * mm, "end": v(-1692.16, 0) * mm});
            skLineSegment(sketch, "E35.top", {"start": v(-3165.36, 2476.5) * mm, "end": v(-1692.16, 2476.5) * mm});
            skLineSegment(sketch, "E35.left", {"start": v(-3165.36, 0) * mm, "end": v(-3165.36, 2476.5) * mm});
            skLineSegment(sketch, "E35.right", {"start": v(-1692.16, 0) * mm, "end": v(-1692.16, 2476.5) * mm});
            skSolve(sketch);
        }
        {
            var Q0;
            Q0=makeQuery(id+"F32.imprint","IMPRINT",FACE,{"disambiguationData":[TD([[makeQuery(id+"F32.imprint","IMPRINT",EDGE,{"derivedFrom":sQuery(id+"F32.wireOp",EDGE,"E35.bottom")}),1.0]])]});
            extrude(context, id + "F33", {"entities" : qUnion([Q0]), "operationType" : NewBodyOperationType.REMOVE, "oppositeDirection" : true, "depth" : 76.2 * mm, "offsetDistance" : 25.4 * mm});
        }
        {
            var Q0;
            {var subQ0=sQuery(id+"F4.wireOp",EDGE,"E8.right");Q0=makeQuery(id+"F22.boolean.opBoolean","MERGE",FACE,{"derivedFrom":[makeQuery(id+"F5.opExtrude","CAP_FACE",FACE,{"disambiguationData":[OSD([sQuery(id+"F4.wireOp",EDGE,"E8.bottom"),sQuery(id+"F4.wireOp",EDGE,"E8.top"),sQuery(id+"F4.wireOp",EDGE,"E8.left"),subQ0])],"isStart":true}),makeQuery(id+"F22.opExtrude","CAP_FACE",FACE,{"disambiguationData":[OSD([sQuery(id+"F2.wireOp",EDGE,"E3"),subQ0,sQuery(id+"F18.wireOp",EDGE,"E29.bottom"),sQuery(id+"F21.wireOp",EDGE,"E30.bottom"),sQuery(id+"F21.wireOp",EDGE,"E30.top"),sQuery(id+"F21.wireOp",EDGE,"E30.right")])],"isStart":false})]});}
            var sketch = newSketch(context, id + "F34", { "sketchPlane" : qUnion([Q0])});
            skLineSegment(sketch, "E36.bottom", {"start": v(1769.95, 3066.13) * mm, "end": v(1160.35, 3066.13) * mm});
            skLineSegment(sketch, "E36.top", {"start": v(1769.95, 3751.93) * mm, "end": v(1160.35, 3751.93) * mm});
            skLineSegment(sketch, "E36.left", {"start": v(1769.95, 3066.13) * mm, "end": v(1769.95, 3751.93) * mm});
            skLineSegment(sketch, "E36.right", {"start": v(1160.35, 3066.13) * mm, "end": v(1160.35, 3751.93) * mm});
            skSolve(sketch);
        }
        {
            var Q0;
            Q0=makeQuery(id+"F34.imprint","IMPRINT",FACE,{"disambiguationData":[TD([[makeQuery(id+"F34.imprint","IMPRINT",EDGE,{"derivedFrom":sQuery(id+"F34.wireOp",EDGE,"E36.bottom")}),-1.0]])]});
            extrude(context, id + "F35", {"entities" : qUnion([Q0]), "oppositeDirection" : true, "depth" : 876.3 * mm, "offsetDistance" : 25.4 * mm});
        }
        {
            var Q0;
            Q0=makeQuery(id+"F3.boolean.opBoolean","MERGE",FACE,{"derivedFrom":[makeQuery(id+"F1.opExtrude","CAP_FACE",FACE,{"disambiguationData":[OSD([sQuery(id+"F0.wireOp",EDGE,"E0.bottom"),sQuery(id+"F0.wireOp",EDGE,"E0.top"),sQuery(id+"F0.wireOp",EDGE,"E0.left"),sQuery(id+"F0.wireOp",EDGE,"E0.right")])],"isStart":true}),makeQuery(id+"F3.opExtrude","CAP_FACE",FACE,{"disambiguationData":[OSD([sQuery(id+"F2.wireOp",EDGE,"E1"),sQuery(id+"F2.wireOp",EDGE,"E2"),sQuery(id+"F2.wireOp",EDGE,"E3"),sQuery(id+"F2.wireOp",EDGE,"E4"),sQuery(id+"F2.wireOp",EDGE,"E5")])],"isStart":true})]});
            var sketch = newSketch(context, id + "F36", { "sketchPlane" : qUnion([Q0])});
            skLineSegment(sketch, "E37", {"start": v(855.55, 316.58) * mm, "end": v(855.55, 926.18) * mm});
            skLineSegment(sketch, "E38", {"start": v(855.55, 926.18) * mm, "end": v(1160.35, 926.18) * mm});
            skLineSegment(sketch, "E39", {"start": v(1160.35, 926.18) * mm, "end": v(1160.35, 1230.98) * mm});
            skLineSegment(sketch, "E40", {"start": v(1160.35, 1230.98) * mm, "end": v(1769.95, 1230.98) * mm});
            skLineSegment(sketch, "E41", {"start": v(1769.95, 1230.98) * mm, "end": v(1769.95, 316.58) * mm});
            skLineSegment(sketch, "E42", {"start": v(1769.95, 316.58) * mm, "end": v(855.55, 316.58) * mm});
            skSolve(sketch);
        }
        {
            var Q0;
            Q0=makeQuery(id+"F36.imprint","IMPRINT",FACE,{"disambiguationData":[TD([[makeQuery(id+"F36.imprint","IMPRINT",EDGE,{"derivedFrom":sQuery(id+"F36.wireOp",EDGE,"E37")}),-1.0]])]});
            var Q1;
            Q1=makeQuery(id+"F35.opExtrude","CAP_FACE",FACE,{"disambiguationData":[OSD([sQuery(id+"F34.wireOp",EDGE,"E36.bottom"),sQuery(id+"F34.wireOp",EDGE,"E36.top"),sQuery(id+"F34.wireOp",EDGE,"E36.left"),sQuery(id+"F34.wireOp",EDGE,"E36.right")])],"isStart":false});
            extrude(context, id + "F37", {"entities" : qUnion([Q0]), "endBound" : BoundingType.UP_TO_SURFACE, "oppositeDirection" : true, "depth" : 25.4 * mm, "endBoundEntityFace" : qUnion([Q1]), "offsetDistance" : 25.4 * mm});
        }
        {
            var Q0;
            Q0=makeQuery(id+"F3.boolean.opBoolean","MERGE",FACE,{"derivedFrom":[makeQuery(id+"F1.opExtrude","CAP_FACE",FACE,{"disambiguationData":[OSD([sQuery(id+"F0.wireOp",EDGE,"E0.bottom"),sQuery(id+"F0.wireOp",EDGE,"E0.top"),sQuery(id+"F0.wireOp",EDGE,"E0.left"),sQuery(id+"F0.wireOp",EDGE,"E0.right")])],"isStart":true}),makeQuery(id+"F3.opExtrude","CAP_FACE",FACE,{"disambiguationData":[OSD([sQuery(id+"F2.wireOp",EDGE,"E1"),sQuery(id+"F2.wireOp",EDGE,"E2"),sQuery(id+"F2.wireOp",EDGE,"E3"),sQuery(id+"F2.wireOp",EDGE,"E4"),sQuery(id+"F2.wireOp",EDGE,"E5")])],"isStart":true})]});
            var sketch = newSketch(context, id + "F38", { "sketchPlane" : qUnion([Q0])});
            skLineSegment(sketch, "E43.bottom", {"start": v(1769.95, 1233.34) * mm, "end": v(1160.35, 1233.34) * mm});
            skLineSegment(sketch, "E43.top", {"start": v(1769.95, 2071.54) * mm, "end": v(1160.35, 2071.54) * mm});
            skLineSegment(sketch, "E43.left", {"start": v(1769.95, 1233.34) * mm, "end": v(1769.95, 2071.54) * mm});
            skLineSegment(sketch, "E43.right", {"start": v(1160.35, 1233.34) * mm, "end": v(1160.35, 2071.54) * mm});
            skSolve(sketch);
        }
        {
            var Q0;
            {var subQ3=sQuery(id+"F38.wireOp",EDGE,"E43.bottom");Q0=makeQuery(id+"F38.imprint","IMPRINT",FACE,{"disambiguationData":[TD([[makeQuery(id+"F38.imprint","IMPRINT",EDGE,{"derivedFrom":subQ3}),-1.0]])]});}
            extrude(context, id + "F39", {"entities" : qUnion([Q0]), "oppositeDirection" : true, "depth" : 2133.6 * mm, "offsetDistance" : 25.4 * mm});
        }
        {
            var Q0;
            Q0=makeQuery(id+"F35.opExtrude","CAP_FACE",FACE,{"disambiguationData":[OSD([sQuery(id+"F34.wireOp",EDGE,"E36.bottom"),sQuery(id+"F34.wireOp",EDGE,"E36.top"),sQuery(id+"F34.wireOp",EDGE,"E36.left"),sQuery(id+"F34.wireOp",EDGE,"E36.right")])],"isStart":true});
            cPlane(context, id + "F40", {"entities" : qUnion([Q0]), "cplaneType" : CPlaneType.OFFSET, "offset" : 1397 * mm, "oppositeDirection" : true, "width" : 152.4 * mm, "height" : 152.4 * mm});
        }
        {
            var Q0;
            Q0=qCreatedBy(id+"F40.planeOp",FACE);
            var sketch = newSketch(context, id + "F41", { "sketchPlane" : qUnion([Q0])});
            skLineSegment(sketch, "E44.bottom", {"start": v(1769.95, 3066.13) * mm, "end": v(1465.15, 3066.13) * mm});
            skLineSegment(sketch, "E44.top", {"start": v(1769.95, 3751.93) * mm, "end": v(1465.15, 3751.93) * mm});
            skLineSegment(sketch, "E44.left", {"start": v(1769.95, 3066.13) * mm, "end": v(1769.95, 3751.93) * mm});
            skLineSegment(sketch, "E44.right", {"start": v(1465.15, 3066.13) * mm, "end": v(1465.15, 3751.93) * mm});
            skSolve(sketch);
        }
        {
            var Q0;
            Q0=makeQuery(id+"F41.imprint","IMPRINT",FACE,{"disambiguationData":[TD([[makeQuery(id+"F41.imprint","IMPRINT",EDGE,{"derivedFrom":sQuery(id+"F41.wireOp",EDGE,"E44.bottom")}),-1.0]])]});
            extrude(context, id + "F42", {"entities" : qUnion([Q0]), "oppositeDirection" : true, "depth" : 1066.8 * mm, "offsetDistance" : 25.4 * mm});
        }
        {
            var Q0;
            Q0=makeQuery(id+"F42.opExtrude","CAP_FACE",FACE,{"disambiguationData":[OSD([sQuery(id+"F41.wireOp",EDGE,"E44.bottom"),sQuery(id+"F41.wireOp",EDGE,"E44.top"),sQuery(id+"F41.wireOp",EDGE,"E44.left"),sQuery(id+"F41.wireOp",EDGE,"E44.right")])],"isStart":false});
            var sketch = newSketch(context, id + "F43", { "sketchPlane" : qUnion([Q0])});
            skLineSegment(sketch, "E45.bottom", {"start": v(1769.95, -1233.34) * mm, "end": v(1465.15, -1233.34) * mm});
            skLineSegment(sketch, "E45.top", {"start": v(1769.95, -928.54) * mm, "end": v(1465.15, -928.54) * mm});
            skLineSegment(sketch, "E45.left", {"start": v(1769.95, -1233.34) * mm, "end": v(1769.95, -928.54) * mm});
            skLineSegment(sketch, "E45.right", {"start": v(1465.15, -1233.34) * mm, "end": v(1465.15, -928.54) * mm});
            skSolve(sketch);
        }
        {
            var Q0;
            Q0=makeQuery(id+"F43.imprint","IMPRINT",FACE,{"disambiguationData":[TD([[makeQuery(id+"F43.imprint","IMPRINT",EDGE,{"derivedFrom":sQuery(id+"F43.wireOp",EDGE,"E45.bottom")}),-1.0]])]});
            var Q1;
            Q1=makeQuery(id+"F42.opExtrude","CAP_FACE",FACE,{"disambiguationData":[OSD([sQuery(id+"F41.wireOp",EDGE,"E44.bottom"),sQuery(id+"F41.wireOp",EDGE,"E44.top"),sQuery(id+"F41.wireOp",EDGE,"E44.left"),sQuery(id+"F41.wireOp",EDGE,"E44.right")])],"isStart":true});
            extrude(context, id + "F44", {"entities" : qUnion([Q0]), "endBound" : BoundingType.UP_TO_SURFACE, "oppositeDirection" : true, "depth" : 25.4 * mm, "endBoundEntityFace" : qUnion([Q1]), "offsetDistance" : 25.4 * mm});
        }
        {
            var Q0;
            Q0=makeQuery(id+"F44.opExtrude","CAP_FACE",FACE,{"disambiguationData":[OSD([sQuery(id+"F43.wireOp",EDGE,"E45.bottom"),sQuery(id+"F43.wireOp",EDGE,"E45.top"),sQuery(id+"F43.wireOp",EDGE,"E45.left"),sQuery(id+"F43.wireOp",EDGE,"E45.right")])],"isStart":true});
            var sketch = newSketch(context, id + "F45", { "sketchPlane" : qUnion([Q0])});
            skLineSegment(sketch, "E46", {"start": v(1769.95, -316.58) * mm, "end": v(1769.95, -926.18) * mm});
            skLineSegment(sketch, "E47", {"start": v(1769.95, -926.18) * mm, "end": v(1465.15, -926.18) * mm});
            skLineSegment(sketch, "E48", {"start": v(1465.15, -926.18) * mm, "end": v(1160.35, -621.38) * mm});
            skLineSegment(sketch, "E49", {"start": v(1160.35, -621.38) * mm, "end": v(1160.35, -316.58) * mm});
            skLineSegment(sketch, "E50", {"start": v(1160.35, -316.58) * mm, "end": v(1769.95, -316.58) * mm});
            skLineSegment(sketch, "E51", {"start": v(1769.95, -316.58) * mm, "end": v(1769.95, -316.58) * mm});
            skSolve(sketch);
        }
        {
            var Q0;
            Q0=makeQuery(id+"F45.imprint","IMPRINT",FACE,{"disambiguationData":[TD([[makeQuery(id+"F45.imprint","IMPRINT",EDGE,{"derivedFrom":sQuery(id+"F45.wireOp",EDGE,"E46")}),-1.0]])]});
            var Q1;
            Q1=makeQuery(id+"F44.opExtrude","CAP_FACE",FACE,{"disambiguationData":[OSD([sQuery(id+"F43.wireOp",EDGE,"E45.bottom"),sQuery(id+"F43.wireOp",EDGE,"E45.top"),sQuery(id+"F43.wireOp",EDGE,"E45.left"),sQuery(id+"F43.wireOp",EDGE,"E45.right")])],"isStart":false});
            extrude(context, id + "F46", {"entities" : qUnion([Q0]), "endBound" : BoundingType.UP_TO_SURFACE, "oppositeDirection" : true, "depth" : 25.4 * mm, "endBoundEntityFace" : qUnion([Q1]), "offsetDistance" : 25.4 * mm});
        }
        {
            var Q0;
            Q0=makeQuery(id+"F46.opExtrude","CAP_FACE",FACE,{"disambiguationData":[OSD([sQuery(id+"F45.wireOp",EDGE,"E46"),sQuery(id+"F45.wireOp",EDGE,"E47"),sQuery(id+"F45.wireOp",EDGE,"E48"),sQuery(id+"F45.wireOp",EDGE,"E49"),sQuery(id+"F45.wireOp",EDGE,"E50")])],"isStart":true});
            var sketch = newSketch(context, id + "F47", { "sketchPlane" : qUnion([Q0])});
            skLineSegment(sketch, "E52.bottom", {"start": v(1160.35, -316.58) * mm, "end": v(855.55, -316.58) * mm});
            skLineSegment(sketch, "E52.top", {"start": v(1160.35, -621.38) * mm, "end": v(855.55, -621.38) * mm});
            skLineSegment(sketch, "E52.left", {"start": v(1160.35, -316.58) * mm, "end": v(1160.35, -621.38) * mm});
            skLineSegment(sketch, "E52.right", {"start": v(855.55, -316.58) * mm, "end": v(855.55, -621.38) * mm});
            skSolve(sketch);
        }
        {
            var Q0;
            Q0=makeQuery(id+"F47.imprint","IMPRINT",FACE,{"disambiguationData":[TD([[makeQuery(id+"F47.imprint","IMPRINT",EDGE,{"derivedFrom":sQuery(id+"F47.wireOp",EDGE,"E52.bottom")}),1.0]])]});
            var Q1;
            Q1=makeQuery(id+"F46.opExtrude","CAP_FACE",FACE,{"disambiguationData":[OSD([sQuery(id+"F45.wireOp",EDGE,"E46"),sQuery(id+"F45.wireOp",EDGE,"E47"),sQuery(id+"F45.wireOp",EDGE,"E48"),sQuery(id+"F45.wireOp",EDGE,"E49"),sQuery(id+"F45.wireOp",EDGE,"E50")])],"isStart":false});
            extrude(context, id + "F48", {"entities" : qUnion([Q0]), "endBound" : BoundingType.UP_TO_SURFACE, "oppositeDirection" : true, "depth" : 25.4 * mm, "endBoundEntityFace" : qUnion([Q1]), "offsetDistance" : 25.4 * mm});
        }
        {
            var Q0;
            Q0=makeQuery(id+"F37.opExtrude","CAP_FACE",FACE,{"disambiguationData":[OSD([sQuery(id+"F36.wireOp",EDGE,"E37"),sQuery(id+"F36.wireOp",EDGE,"E38"),sQuery(id+"F36.wireOp",EDGE,"E39"),sQuery(id+"F36.wireOp",EDGE,"E40"),sQuery(id+"F36.wireOp",EDGE,"E41"),sQuery(id+"F36.wireOp",EDGE,"E42")])],"isStart":false});
            var sketch = newSketch(context, id + "F49", { "sketchPlane" : qUnion([Q0])});
            skLineSegment(sketch, "E53.bottom", {"start": v(855.55, -316.58) * mm, "end": v(169.75, -316.58) * mm});
            skLineSegment(sketch, "E53.top", {"start": v(855.55, -926.18) * mm, "end": v(169.75, -926.18) * mm});
            skLineSegment(sketch, "E53.left", {"start": v(855.55, -316.58) * mm, "end": v(855.55, -926.18) * mm});
            skLineSegment(sketch, "E53.right", {"start": v(169.75, -316.58) * mm, "end": v(169.75, -926.18) * mm});
            skSolve(sketch);
        }
        {
            var Q0;
            Q0=makeQuery(id+"F49.imprint","IMPRINT",FACE,{"disambiguationData":[TD([[makeQuery(id+"F49.imprint","IMPRINT",EDGE,{"derivedFrom":sQuery(id+"F49.wireOp",EDGE,"E53.bottom")}),1.0]])]});
            var Q1;
            Q1=makeQuery(id+"F37.opExtrude","CAP_FACE",FACE,{"disambiguationData":[OSD([sQuery(id+"F36.wireOp",EDGE,"E37"),sQuery(id+"F36.wireOp",EDGE,"E38"),sQuery(id+"F36.wireOp",EDGE,"E39"),sQuery(id+"F36.wireOp",EDGE,"E40"),sQuery(id+"F36.wireOp",EDGE,"E41"),sQuery(id+"F36.wireOp",EDGE,"E42")])],"isStart":true});
            extrude(context, id + "F50", {"entities" : qUnion([Q0]), "endBound" : BoundingType.UP_TO_SURFACE, "oppositeDirection" : true, "depth" : 25.4 * mm, "endBoundEntityFace" : qUnion([Q1]), "offsetDistance" : 25.4 * mm});
        }
        {
            var Q0;
            Q0=makeQuery(id+"F50.opExtrude","CAP_FACE",FACE,{"disambiguationData":[OSD([sQuery(id+"F49.wireOp",EDGE,"E53.bottom"),sQuery(id+"F49.wireOp",EDGE,"E53.top"),sQuery(id+"F49.wireOp",EDGE,"E53.left"),sQuery(id+"F49.wireOp",EDGE,"E53.right")])],"isStart":true});
            var sketch = newSketch(context, id + "F51", { "sketchPlane" : qUnion([Q0])});
            skLineSegment(sketch, "E54.bottom", {"start": v(169.75, -316.58) * mm, "end": v(-744.65, -316.58) * mm});
            skLineSegment(sketch, "E54.top", {"start": v(169.75, -926.18) * mm, "end": v(-744.65, -926.18) * mm});
            skLineSegment(sketch, "E54.left", {"start": v(169.75, -316.58) * mm, "end": v(169.75, -926.18) * mm});
            skLineSegment(sketch, "E54.right", {"start": v(-744.65, -316.58) * mm, "end": v(-744.65, -926.18) * mm});
            skSolve(sketch);
        }
        {
            var Q0;
            Q0=makeQuery(id+"F51.imprint","IMPRINT",FACE,{"disambiguationData":[TD([[makeQuery(id+"F51.imprint","IMPRINT",EDGE,{"derivedFrom":sQuery(id+"F51.wireOp",EDGE,"E54.bottom")}),1.0]])]});
            var Q1;
            Q1=makeQuery(id+"F50.opExtrude","CAP_FACE",FACE,{"disambiguationData":[OSD([sQuery(id+"F49.wireOp",EDGE,"E53.bottom"),sQuery(id+"F49.wireOp",EDGE,"E53.top"),sQuery(id+"F49.wireOp",EDGE,"E53.left"),sQuery(id+"F49.wireOp",EDGE,"E53.right")])],"isStart":false});
            extrude(context, id + "F52", {"entities" : qUnion([Q0]), "endBound" : BoundingType.UP_TO_SURFACE, "oppositeDirection" : true, "depth" : 25.4 * mm, "endBoundEntityFace" : qUnion([Q1]), "offsetDistance" : 25.4 * mm});
        }
        {
            var Q0;
            Q0=makeQuery(id+"F52.opExtrude","CAP_FACE",FACE,{"disambiguationData":[OSD([sQuery(id+"F51.wireOp",EDGE,"E54.bottom"),sQuery(id+"F51.wireOp",EDGE,"E54.top"),sQuery(id+"F51.wireOp",EDGE,"E54.left"),sQuery(id+"F51.wireOp",EDGE,"E54.right")])],"isStart":true});
            var sketch = newSketch(context, id + "F53", { "sketchPlane" : qUnion([Q0])});
            skLineSegment(sketch, "E55.bottom", {"start": v(-744.65, -316.58) * mm, "end": v(-1430.45, -316.58) * mm});
            skLineSegment(sketch, "E55.top", {"start": v(-744.65, -926.18) * mm, "end": v(-1430.45, -926.18) * mm});
            skLineSegment(sketch, "E55.left", {"start": v(-744.65, -316.58) * mm, "end": v(-744.65, -926.18) * mm});
            skLineSegment(sketch, "E55.right", {"start": v(-1430.45, -316.58) * mm, "end": v(-1430.45, -926.18) * mm});
            skSolve(sketch);
        }
        {
            var Q0;
            Q0=makeQuery(id+"F53.imprint","IMPRINT",FACE,{"disambiguationData":[TD([[makeQuery(id+"F53.imprint","IMPRINT",EDGE,{"derivedFrom":sQuery(id+"F53.wireOp",EDGE,"E55.bottom")}),1.0]])]});
            var Q1;
            Q1=makeQuery(id+"F52.opExtrude","CAP_FACE",FACE,{"disambiguationData":[OSD([sQuery(id+"F51.wireOp",EDGE,"E54.bottom"),sQuery(id+"F51.wireOp",EDGE,"E54.top"),sQuery(id+"F51.wireOp",EDGE,"E54.left"),sQuery(id+"F51.wireOp",EDGE,"E54.right")])],"isStart":false});
            extrude(context, id + "F54", {"entities" : qUnion([Q0]), "endBound" : BoundingType.UP_TO_SURFACE, "oppositeDirection" : true, "depth" : 25.4 * mm, "endBoundEntityFace" : qUnion([Q1]), "offsetDistance" : 25.4 * mm});
        }
        {
            var Q0;
            Q0=makeQuery(id+"F48.opExtrude","CAP_FACE",FACE,{"disambiguationData":[OSD([sQuery(id+"F47.wireOp",EDGE,"E52.bottom"),sQuery(id+"F47.wireOp",EDGE,"E52.top"),sQuery(id+"F47.wireOp",EDGE,"E52.left"),sQuery(id+"F47.wireOp",EDGE,"E52.right")])],"isStart":true});
            var sketch = newSketch(context, id + "F55", { "sketchPlane" : qUnion([Q0])});
            skLineSegment(sketch, "E56.bottom", {"start": v(855.55, -316.58) * mm, "end": v(169.75, -316.58) * mm});
            skLineSegment(sketch, "E56.top", {"start": v(855.55, -621.38) * mm, "end": v(169.75, -621.38) * mm});
            skLineSegment(sketch, "E56.left", {"start": v(855.55, -316.58) * mm, "end": v(855.55, -621.38) * mm});
            skLineSegment(sketch, "E56.right", {"start": v(169.75, -316.58) * mm, "end": v(169.75, -621.38) * mm});
            skSolve(sketch);
        }
        {
            var Q0;
            Q0=makeQuery(id+"F55.imprint","IMPRINT",FACE,{"disambiguationData":[TD([[makeQuery(id+"F55.imprint","IMPRINT",EDGE,{"derivedFrom":sQuery(id+"F55.wireOp",EDGE,"E56.bottom")}),1.0]])]});
            var Q1;
            Q1=makeQuery(id+"F48.opExtrude","CAP_FACE",FACE,{"disambiguationData":[OSD([sQuery(id+"F47.wireOp",EDGE,"E52.bottom"),sQuery(id+"F47.wireOp",EDGE,"E52.top"),sQuery(id+"F47.wireOp",EDGE,"E52.left"),sQuery(id+"F47.wireOp",EDGE,"E52.right")])],"isStart":false});
            extrude(context, id + "F56", {"entities" : qUnion([Q0]), "endBound" : BoundingType.UP_TO_SURFACE, "oppositeDirection" : true, "depth" : 25.4 * mm, "endBoundEntityFace" : qUnion([Q1]), "offsetDistance" : 25.4 * mm});
        }
        {
            var Q0;
            Q0=makeQuery(id+"F56.opExtrude","CAP_FACE",FACE,{"disambiguationData":[OSD([sQuery(id+"F55.wireOp",EDGE,"E56.bottom"),sQuery(id+"F55.wireOp",EDGE,"E56.top"),sQuery(id+"F55.wireOp",EDGE,"E56.left"),sQuery(id+"F55.wireOp",EDGE,"E56.right")])],"isStart":true});
            var sketch = newSketch(context, id + "F57", { "sketchPlane" : qUnion([Q0])});
            skLineSegment(sketch, "E57.bottom", {"start": v(169.75, -316.58) * mm, "end": v(-744.65, -316.58) * mm});
            skLineSegment(sketch, "E57.top", {"start": v(169.75, -621.38) * mm, "end": v(-744.65, -621.38) * mm});
            skLineSegment(sketch, "E57.left", {"start": v(169.75, -316.58) * mm, "end": v(169.75, -621.38) * mm});
            skLineSegment(sketch, "E57.right", {"start": v(-744.65, -316.58) * mm, "end": v(-744.65, -621.38) * mm});
            skSolve(sketch);
        }
        {
            var Q0;
            Q0=makeQuery(id+"F57.imprint","IMPRINT",FACE,{"disambiguationData":[TD([[makeQuery(id+"F57.imprint","IMPRINT",EDGE,{"derivedFrom":sQuery(id+"F57.wireOp",EDGE,"E57.bottom")}),1.0]])]});
            extrude(context, id + "F58", {"entities" : qUnion([Q0]), "oppositeDirection" : true, "depth" : 381 * mm, "offsetDistance" : 25.4 * mm});
        }
        {
            var Q0;
            Q0=makeQuery(id+"F58.opExtrude","CAP_FACE",FACE,{"disambiguationData":[OSD([sQuery(id+"F57.wireOp",EDGE,"E57.bottom"),sQuery(id+"F57.wireOp",EDGE,"E57.top"),sQuery(id+"F57.wireOp",EDGE,"E57.left"),sQuery(id+"F57.wireOp",EDGE,"E57.right")])],"isStart":true});
            var sketch = newSketch(context, id + "F59", { "sketchPlane" : qUnion([Q0])});
            skLineSegment(sketch, "E58.bottom", {"start": v(-744.65, -316.58) * mm, "end": v(-1430.45, -316.58) * mm});
            skLineSegment(sketch, "E58.top", {"start": v(-744.65, -621.38) * mm, "end": v(-1430.45, -621.38) * mm});
            skLineSegment(sketch, "E58.left", {"start": v(-744.65, -316.58) * mm, "end": v(-744.65, -621.38) * mm});
            skLineSegment(sketch, "E58.right", {"start": v(-1430.45, -316.58) * mm, "end": v(-1430.45, -621.38) * mm});
            skSolve(sketch);
        }
        {
            var Q0;
            Q0=makeQuery(id+"F59.imprint","IMPRINT",FACE,{"disambiguationData":[TD([[makeQuery(id+"F59.imprint","IMPRINT",EDGE,{"derivedFrom":sQuery(id+"F59.wireOp",EDGE,"E58.bottom")}),1.0]])]});
            var Q1;
            Q1=makeQuery(id+"F56.opExtrude","CAP_FACE",FACE,{"disambiguationData":[OSD([sQuery(id+"F55.wireOp",EDGE,"E56.bottom"),sQuery(id+"F55.wireOp",EDGE,"E56.top"),sQuery(id+"F55.wireOp",EDGE,"E56.left"),sQuery(id+"F55.wireOp",EDGE,"E56.right")])],"isStart":false});
            extrude(context, id + "F60", {"entities" : qUnion([Q0]), "endBound" : BoundingType.UP_TO_SURFACE, "oppositeDirection" : true, "depth" : 25.4 * mm, "endBoundEntityFace" : qUnion([Q1]), "offsetDistance" : 25.4 * mm});
        }
        {
            var Q0;
            Q0=makeQuery(id+"F39.opExtrude","CAP_FACE",FACE,{"disambiguationData":[OSD([sQuery(id+"F38.wireOp",EDGE,"E43.bottom"),sQuery(id+"F38.wireOp",EDGE,"E43.top"),sQuery(id+"F38.wireOp",EDGE,"E43.left"),sQuery(id+"F38.wireOp",EDGE,"E43.right")])],"isStart":false});
            extrude(context, id + "F61", {"entities" : qUnion([Q0]), "depth" : 381 * mm, "offsetDistance" : 25.4 * mm});
        }
        {
            var Q0;
            Q0=makeQuery(id+"F37.opExtrude","CAP_FACE",FACE,{"disambiguationData":[OSD([sQuery(id+"F36.wireOp",EDGE,"E37"),sQuery(id+"F36.wireOp",EDGE,"E38"),sQuery(id+"F36.wireOp",EDGE,"E39"),sQuery(id+"F36.wireOp",EDGE,"E40"),sQuery(id+"F36.wireOp",EDGE,"E41"),sQuery(id+"F36.wireOp",EDGE,"E42")])],"isStart":true});
            var sketch = newSketch(context, id + "F62", { "sketchPlane" : qUnion([Q0])});
            skLineSegment(sketch, "E59.bottom", {"start": v(-58.85, 1967.58) * mm, "end": v(-668.45, 1967.58) * mm});
            skLineSegment(sketch, "E59.top", {"start": v(-58.85, 2881.98) * mm, "end": v(-668.45, 2881.98) * mm});
            skLineSegment(sketch, "E59.left", {"start": v(-58.85, 1967.58) * mm, "end": v(-58.85, 2881.98) * mm});
            skLineSegment(sketch, "E59.right", {"start": v(-668.45, 1967.58) * mm, "end": v(-668.45, 2881.98) * mm});
            skSolve(sketch);
        }
        {
            var Q0;
            Q0=makeQuery(id+"F62.imprint","IMPRINT",FACE,{"disambiguationData":[TD([[makeQuery(id+"F62.imprint","IMPRINT",EDGE,{"derivedFrom":sQuery(id+"F62.wireOp",EDGE,"E59.bottom")}),-1.0]])]});
            extrude(context, id + "F63", {"entities" : qUnion([Q0]), "oppositeDirection" : true, "depth" : 876.3 * mm, "offsetDistance" : 25.4 * mm});
        }
        {
            var Q0;
            Q0=makeQuery(id+"F63.opExtrude","CAP_FACE",FACE,{"disambiguationData":[OSD([sQuery(id+"F62.wireOp",EDGE,"E59.bottom"),sQuery(id+"F62.wireOp",EDGE,"E59.top"),sQuery(id+"F62.wireOp",EDGE,"E59.left"),sQuery(id+"F62.wireOp",EDGE,"E59.right")])],"isStart":true});
            var sketch = newSketch(context, id + "F64", { "sketchPlane" : qUnion([Q0])});
            skLineSegment(sketch, "E60", {"start": v(-58.85, 1967.58) * mm, "end": v(-8.05, 1967.58) * mm});
            skLineSegment(sketch, "E61", {"start": v(-8.05, 1967.58) * mm, "end": v(-8.05, 1840.58) * mm});
            skLineSegment(sketch, "E62", {"start": v(-8.05, 1840.58) * mm, "end": v(-795.45, 1840.58) * mm});
            skLineSegment(sketch, "E63", {"start": v(-795.45, 1840.58) * mm, "end": v(-795.45, 3618.58) * mm});
            skLineSegment(sketch, "E64", {"start": v(-795.45, 3618.58) * mm, "end": v(-8.05, 3618.58) * mm});
            skLineSegment(sketch, "E65", {"start": v(-8.05, 3618.58) * mm, "end": v(-8.05, 3491.58) * mm});
            skLineSegment(sketch, "E66", {"start": v(-8.05, 3491.58) * mm, "end": v(-668.45, 3491.58) * mm});
            skLineSegment(sketch, "E67", {"start": v(-668.45, 3491.58) * mm, "end": v(-668.45, 1967.58) * mm});
            skLineSegment(sketch, "E68", {"start": v(-668.45, 1967.58) * mm, "end": v(-58.85, 1967.58) * mm});
            skSolve(sketch);
        }
        {
            var Q0;
            Q0=makeQuery(id+"F64.imprint","IMPRINT",FACE,{"disambiguationData":[TD([[makeQuery(id+"F64.imprint","IMPRINT",EDGE,{"derivedFrom":sQuery(id+"F64.wireOp",EDGE,"E60")}),-1.0]])]});
            var Q1;
            Q1=makeQuery(id+"F63.opExtrude","CAP_FACE",FACE,{"disambiguationData":[OSD([sQuery(id+"F62.wireOp",EDGE,"E59.bottom"),sQuery(id+"F62.wireOp",EDGE,"E59.top"),sQuery(id+"F62.wireOp",EDGE,"E59.left"),sQuery(id+"F62.wireOp",EDGE,"E59.right")])],"isStart":false});
            extrude(context, id + "F65", {"entities" : qUnion([Q0]), "endBound" : BoundingType.UP_TO_SURFACE, "oppositeDirection" : true, "depth" : 25.4 * mm, "endBoundEntityFace" : qUnion([Q1]), "offsetDistance" : 25.4 * mm});
        }
        {
            var Q0;
            Q0=makeQuery(id+"F63.opExtrude","CAP_FACE",FACE,{"disambiguationData":[OSD([sQuery(id+"F62.wireOp",EDGE,"E59.bottom"),sQuery(id+"F62.wireOp",EDGE,"E59.top"),sQuery(id+"F62.wireOp",EDGE,"E59.left"),sQuery(id+"F62.wireOp",EDGE,"E59.right")])],"isStart":false});
            cPlane(context, id + "F66", {"entities" : qUnion([Q0]), "cplaneType" : CPlaneType.OFFSET, "offset" : 0 * mm, "width" : 152.4 * mm, "height" : 152.4 * mm});
        }
        {
            var Q0;
            Q0=qCreatedBy(id+"F66.planeOp",FACE);
            var sketch = newSketch(context, id + "F67", { "sketchPlane" : qUnion([Q0])});
            skLineSegment(sketch, "E69.bottom", {"start": v(30.05, -3872.58) * mm, "end": v(-1862.25, -3872.58) * mm});
            skLineSegment(sketch, "E69.top", {"start": v(30.05, -1802.48) * mm, "end": v(-1862.25, -1802.48) * mm});
            skLineSegment(sketch, "E69.left", {"start": v(30.05, -3872.58) * mm, "end": v(30.05, -1802.48) * mm});
            skLineSegment(sketch, "E69.right", {"start": v(-1862.25, -3872.58) * mm, "end": v(-1862.25, -1802.48) * mm});
            skSolve(sketch);
        }
        {
            var Q0;
            Q0=makeQuery(id+"F67.imprint","IMPRINT",FACE,{"disambiguationData":[TD([[makeQuery(id+"F67.imprint","IMPRINT",EDGE,{"derivedFrom":sQuery(id+"F67.wireOp",EDGE,"E69.bottom")}),-1.0]])]});
            extrude(context, id + "F68", {"entities" : qUnion([Q0]), "depth" : 38.1 * mm, "offsetDistance" : 25.4 * mm});
        }
        {
            var Q0;
            {var subQ0=sQuery(id+"F6.wireOp",EDGE,"E10.bottom");Q0=makeQuery(id+"F13.boolean.opBoolean","MERGE",FACE,{"derivedFrom":[makeQuery(id+"F11.boolean.opBoolean","MERGE",FACE,{"derivedFrom":[makeQuery(id+"F9.boolean.opBoolean","MERGE",FACE,{"derivedFrom":[makeQuery(id+"F7.opExtrude","CAP_FACE",FACE,{"disambiguationData":[OSD([subQ0,sQuery(id+"F6.wireOp",EDGE,"E10.top"),sQuery(id+"F6.wireOp",EDGE,"E10.left"),sQuery(id+"F6.wireOp",EDGE,"E10.right")])],"isStart":true}),makeQuery(id+"F9.opExtrude","CAP_FACE",FACE,{"disambiguationData":[OSD([subQ0,sQuery(id+"F8.wireOp",EDGE,"E11.left"),sQuery(id+"F8.wireOp",EDGE,"E11.right"),sQuery(id+"F8.wireOp",EDGE,"E12.bottom"),sQuery(id+"F8.wireOp",EDGE,"E12.top"),sQuery(id+"F8.wireOp",EDGE,"E12.left"),sQuery(id+"F8.wireOp",EDGE,"E13"),sQuery(id+"F8.wireOp",EDGE,"E14"),sQuery(id+"F8.wireOp",EDGE,"E16"),sQuery(id+"F8.wireOp",EDGE,"E17"),sQuery(id+"F8.wireOp",EDGE,"E18"),sQuery(id+"F8.wireOp",EDGE,"E19"),sQuery(id+"F8.wireOp",EDGE,"E20"),sQuery(id+"F8.wireOp",EDGE,"E21"),sQuery(id+"F8.wireOp",EDGE,"E22"),sQuery(id+"F8.wireOp",EDGE,"E23"),sQuery(id+"F8.wireOp",EDGE,"E24")])],"isStart":true})]}),makeQuery(id+"F11.opExtrude","CAP_FACE",FACE,{"disambiguationData":[OSD([sQuery(id+"F10.wireOp",EDGE,"E25.bottom"),sQuery(id+"F10.wireOp",EDGE,"E25.top"),sQuery(id+"F10.wireOp",EDGE,"E25.left"),sQuery(id+"F10.wireOp",EDGE,"E25.right")])],"isStart":true})]}),makeQuery(id+"F13.opExtrude","SWEPT_FACE",FACE,{"disambiguationData":[OSD([sQuery(id+"F12.wireOp",EDGE,"E26.bottom")])]})]});}
            var sketch = newSketch(context, id + "F69", { "sketchPlane" : qUnion([Q0])});
            skLineSegment(sketch, "E70.bottom", {"start": v(747.6, 5834.73) * mm, "end": v(-154.1, 5834.73) * mm});
            skLineSegment(sketch, "E70.top", {"start": v(747.6, 5079.08) * mm, "end": v(-154.1, 5079.08) * mm});
            skLineSegment(sketch, "E70.left", {"start": v(747.6, 5834.73) * mm, "end": v(747.6, 5079.08) * mm});
            skLineSegment(sketch, "E70.right", {"start": v(-154.1, 5834.73) * mm, "end": v(-154.1, 5079.08) * mm});
            skSolve(sketch);
        }
        {
            var Q0;
            Q0=makeQuery(id+"F69.imprint","IMPRINT",FACE,{"disambiguationData":[TD([[makeQuery(id+"F69.imprint","IMPRINT",EDGE,{"derivedFrom":sQuery(id+"F69.wireOp",EDGE,"E70.bottom")}),1.0]])]});
            extrude(context, id + "F70", {"entities" : qUnion([Q0]), "oppositeDirection" : true, "depth" : 1752.6 * mm, "offsetDistance" : 25.4 * mm});
        }
        {
            var Q0;
            {var subQ0=sQuery(id+"F6.wireOp",EDGE,"E10.bottom");Q0=makeQuery(id+"F13.boolean.opBoolean","MERGE",FACE,{"derivedFrom":[makeQuery(id+"F11.boolean.opBoolean","MERGE",FACE,{"derivedFrom":[makeQuery(id+"F9.boolean.opBoolean","MERGE",FACE,{"derivedFrom":[makeQuery(id+"F7.opExtrude","CAP_FACE",FACE,{"disambiguationData":[OSD([subQ0,sQuery(id+"F6.wireOp",EDGE,"E10.top"),sQuery(id+"F6.wireOp",EDGE,"E10.left"),sQuery(id+"F6.wireOp",EDGE,"E10.right")])],"isStart":true}),makeQuery(id+"F9.opExtrude","CAP_FACE",FACE,{"disambiguationData":[OSD([subQ0,sQuery(id+"F8.wireOp",EDGE,"E11.left"),sQuery(id+"F8.wireOp",EDGE,"E11.right"),sQuery(id+"F8.wireOp",EDGE,"E12.bottom"),sQuery(id+"F8.wireOp",EDGE,"E12.top"),sQuery(id+"F8.wireOp",EDGE,"E12.left"),sQuery(id+"F8.wireOp",EDGE,"E13"),sQuery(id+"F8.wireOp",EDGE,"E14"),sQuery(id+"F8.wireOp",EDGE,"E16"),sQuery(id+"F8.wireOp",EDGE,"E17"),sQuery(id+"F8.wireOp",EDGE,"E18"),sQuery(id+"F8.wireOp",EDGE,"E19"),sQuery(id+"F8.wireOp",EDGE,"E20"),sQuery(id+"F8.wireOp",EDGE,"E21"),sQuery(id+"F8.wireOp",EDGE,"E22"),sQuery(id+"F8.wireOp",EDGE,"E23"),sQuery(id+"F8.wireOp",EDGE,"E24")])],"isStart":true})]}),makeQuery(id+"F11.opExtrude","CAP_FACE",FACE,{"disambiguationData":[OSD([sQuery(id+"F10.wireOp",EDGE,"E25.bottom"),sQuery(id+"F10.wireOp",EDGE,"E25.top"),sQuery(id+"F10.wireOp",EDGE,"E25.left"),sQuery(id+"F10.wireOp",EDGE,"E25.right")])],"isStart":true})]}),makeQuery(id+"F13.opExtrude","SWEPT_FACE",FACE,{"disambiguationData":[OSD([sQuery(id+"F12.wireOp",EDGE,"E26.bottom")])]})]});}
            var sketch = newSketch(context, id + "F71", { "sketchPlane" : qUnion([Q0])});
            skLineSegment(sketch, "E71.bottom", {"start": v(-160.45, 5834.73) * mm, "end": v(-541.45, 5834.73) * mm});
            skLineSegment(sketch, "E71.top", {"start": v(-160.45, 5225.13) * mm, "end": v(-541.45, 5225.13) * mm});
            skLineSegment(sketch, "E71.left", {"start": v(-160.45, 5834.73) * mm, "end": v(-160.45, 5225.13) * mm});
            skLineSegment(sketch, "E71.right", {"start": v(-541.45, 5834.73) * mm, "end": v(-541.45, 5225.13) * mm});
            skSolve(sketch);
        }
        {
            var Q0;
            Q0=makeQuery(id+"F71.imprint","IMPRINT",FACE,{"disambiguationData":[TD([[makeQuery(id+"F71.imprint","IMPRINT",EDGE,{"derivedFrom":sQuery(id+"F71.wireOp",EDGE,"E71.bottom")}),1.0]])]});
            extrude(context, id + "F72", {"entities" : qUnion([Q0]), "oppositeDirection" : true, "depth" : 876.3 * mm, "offsetDistance" : 25.4 * mm});
        }
        {
            var Q0;
            Q0=makeQuery(id+"F42.opExtrude","CAP_FACE",FACE,{"disambiguationData":[OSD([sQuery(id+"F41.wireOp",EDGE,"E44.bottom"),sQuery(id+"F41.wireOp",EDGE,"E44.top"),sQuery(id+"F41.wireOp",EDGE,"E44.left"),sQuery(id+"F41.wireOp",EDGE,"E44.right")])],"isStart":false});
            var sketch = newSketch(context, id + "F73", { "sketchPlane" : qUnion([Q0])});
            skLineSegment(sketch, "E72.bottom", {"start": v(753.95, -5834.73) * mm, "end": v(-160.45, -5834.73) * mm});
            skLineSegment(sketch, "E72.top", {"start": v(753.95, -5225.13) * mm, "end": v(-160.45, -5225.13) * mm});
            skLineSegment(sketch, "E72.left", {"start": v(753.95, -5834.73) * mm, "end": v(753.95, -5225.13) * mm});
            skLineSegment(sketch, "E72.right", {"start": v(-160.45, -5834.73) * mm, "end": v(-160.45, -5225.13) * mm});
            skSolve(sketch);
        }
        {
            var Q0;
            Q0=makeQuery(id+"F73.imprint","IMPRINT",FACE,{"disambiguationData":[TD([[makeQuery(id+"F73.imprint","IMPRINT",EDGE,{"derivedFrom":sQuery(id+"F73.wireOp",EDGE,"E72.bottom")}),-1.0]])]});
            extrude(context, id + "F74", {"entities" : qUnion([Q0]), "oppositeDirection" : true, "depth" : 609.6 * mm, "offsetDistance" : 25.4 * mm});
        }
        {
            var Q0;
            Q0=makeQuery(id+"F74.opExtrude","CAP_FACE",FACE,{"disambiguationData":[OSD([sQuery(id+"F73.wireOp",EDGE,"E72.bottom"),sQuery(id+"F73.wireOp",EDGE,"E72.top"),sQuery(id+"F73.wireOp",EDGE,"E72.left"),sQuery(id+"F73.wireOp",EDGE,"E72.right")])],"isStart":true});
            var sketch = newSketch(context, id + "F75", { "sketchPlane" : qUnion([Q0])});
            skLineSegment(sketch, "E73.bottom", {"start": v(-160.45, -5834.73) * mm, "end": v(-541.45, -5834.73) * mm});
            skLineSegment(sketch, "E73.top", {"start": v(-160.45, -5529.93) * mm, "end": v(-541.45, -5529.93) * mm});
            skLineSegment(sketch, "E73.left", {"start": v(-160.45, -5834.73) * mm, "end": v(-160.45, -5529.93) * mm});
            skLineSegment(sketch, "E73.right", {"start": v(-541.45, -5834.73) * mm, "end": v(-541.45, -5529.93) * mm});
            skSolve(sketch);
        }
        {
            var Q0;
            Q0=makeQuery(id+"F75.imprint","IMPRINT",FACE,{"disambiguationData":[TD([[makeQuery(id+"F75.imprint","IMPRINT",EDGE,{"derivedFrom":sQuery(id+"F75.wireOp",EDGE,"E73.bottom")}),-1.0]])]});
            var Q1;
            Q1=makeQuery(id+"F42.opExtrude","CAP_FACE",FACE,{"disambiguationData":[OSD([sQuery(id+"F41.wireOp",EDGE,"E44.bottom"),sQuery(id+"F41.wireOp",EDGE,"E44.top"),sQuery(id+"F41.wireOp",EDGE,"E44.left"),sQuery(id+"F41.wireOp",EDGE,"E44.right")])],"isStart":true});
            extrude(context, id + "F76", {"entities" : qUnion([Q0]), "endBound" : BoundingType.UP_TO_SURFACE, "oppositeDirection" : true, "depth" : 25.4 * mm, "endBoundEntityFace" : qUnion([Q1]), "offsetDistance" : 25.4 * mm});
        }
    });
